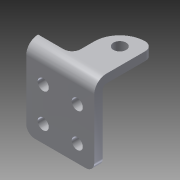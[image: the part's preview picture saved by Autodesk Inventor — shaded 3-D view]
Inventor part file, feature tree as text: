
AUTODESK INVENTOR PART (.ipt)
format: ipt  version: 2014 (Build 180170000, 170)  size: 216,576 bytes
history: native  units: in
note: dims shown in document units (in); Inventor stores cm internally (conversion verified against a paired STEP export)
features: sheet_metal_op x4, sketch x3, other x3, extrude x1, fillet x1
ambient origin geometry x8: Origin, YZ Plane, XZ Plane, XY Plane, X Axis, Y Axis, Z Axis, Center Point
bodies: Solid1 (feature_tree)
feature tree (12):
  sheet_metal_op  "Face1"
  sheet_metal_op  "Flange1"
  extrude  "Extrusion1"  Depth=1.0in
  fillet  "Fillet1"  Radius=0.163in
  sketch  "Sketch1"  dims[d0=1.0in d1=1.0in d2=0.163in]
  other  "Plate1"
  sketch  "Sketch2"  dims[d3=0.25in]
  other  "Plate2"
  sheet_metal_op  "Bend1"
  sheet_metal_op  "Corner1"
  sketch  "Sketch3"  dims[d4=0.25in d5=0.7874in d7=0.5in d8=0.7874in d10=0.5in d13=0.125in d14=0.125in d15=0.0625in d16=0.25in d17=0.125in d18=0.875in d19=90.0deg d20=0.05in d21=0.5in d22=0.125in d23=0.125in d24=0.187in d25=0.25in d26=0.25in d27=0.375in d28=0.125in d29=1.0in d30=0.0in d31=0.125in]
  other  "Definition1"
